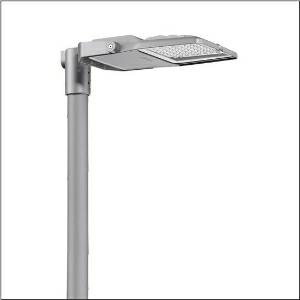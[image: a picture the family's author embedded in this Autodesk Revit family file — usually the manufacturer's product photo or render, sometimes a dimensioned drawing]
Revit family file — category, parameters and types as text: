
# Revit family: floodlight_fl_21_mini___pl64_5xa7772b2e3a_9ae7
name_source: partatom
category: Lighting Fixtures
units: mm (PartAtom-declared; Revit-internal decimal feet)

## family parameters
Cut with Voids When Loaded = No
Host = Face
Light Source = No
Part Type = Normal
Room Calculation Point = No
Round Connector Dimension = Use Diameter
Shared = No

## types (1)
- --- (1 x LED, 6020 lm, 45.5 W, 3000K)
    Apparent Load = 46 VA
    CIE Flux Codes = 28 80 98 100 100
    Color Rendering = 70
    Color Temperature = 3000K
    Default Elevation = 1800 mm
    Description = Floodlight FL 21 mini, floodlight, primary light control with lens, of PMMA, primary optical cover: protective disc, of toughened safety glass, transparent, light distribution: PL64, light emission: direct distribution, installation type: surface-mounted, LED, High Power LED, rated luminous flux: 6.020lm, luminous efficacy: 132lm/W, light colour: 730, colour temperature: 3000K, control gear: ECG iQ, control: Auto-Match, Temp-Guard, Night-Set, Smart-Wire, Desk-Remote (wireless, voltage-free reading and setting of iQ features in the workshop via application-optimized NFC function/RFID function), optimised constant luminous flux control (CLO 2.0), Light-Fading, Lumen-Switch, with terminal, 6-pole, mains connection: 220..240V, AC, 50/60Hz, start of lifetime: 46W, end of lifetime: 48W, reduction: 22W, luminaire housing, of diecast aluminium, powder-coated, Siteco® metallic grey (DB 702S), corrosivity category C5 according to DIN EN ISO 12944, mast bracket, of steel, galvanised, powder-coated, protection rating (complete): IP66, insulation class (complete): insulation class II (safety insulation), certification: CE, ENEC, VDE, protection symbol: D, impact resistance: IK08, permissible operating ambient temperature: -40..+40°C, permissible operating ambient temperature for outdoor applications: -40..+50°C, standard: DIN EN 12944, packaging unit: 1 piece

Light Distribution: PL64
    Height = 70 mm
    Lamp = 1 x LED
    Lamp Light Flux = 6020 lm
    Lamp Power = 45.5 W
    Lamp count = 1
    Length = 485 mm
    Luminous efficacy = 132 lm/W
    Manufacturer = Siteco
    ModVariant = No
    Model = 5XA7772B2E3A
    Number of Poles = 1
    OnlyDefault = Yes
    Power Factor = 1
    Product Name = Floodlight FL 21 mini | PL64
    Product group = floodlight | pylon top
    ProductGroupID = 6101
    Protection Class = Protection class II
    Protection Degree = IP 66
    RLX_Detail_Level = 1
    RlxData = <blob elided: 101073 chars, md5=634fafae>
    Socket = socket
    Standby Power = 0 W
    System Light Flux = 6020 lm
    System Power = 46 W
    Type Comments = factory setting: luminous flux: 100 % | dim-lin: 254 | 463 mA
    Type Image = l_1007125.jpg
    URL = http://relux.com
    VarID = @adj_077953
    Voltage = 0 V
    Weight = 0.00 kg
    Width = 337 mm

## geometry (parser evidence)
native form markers: Blend x4, Sweep x11
no freeform markers — native parametric forms only
